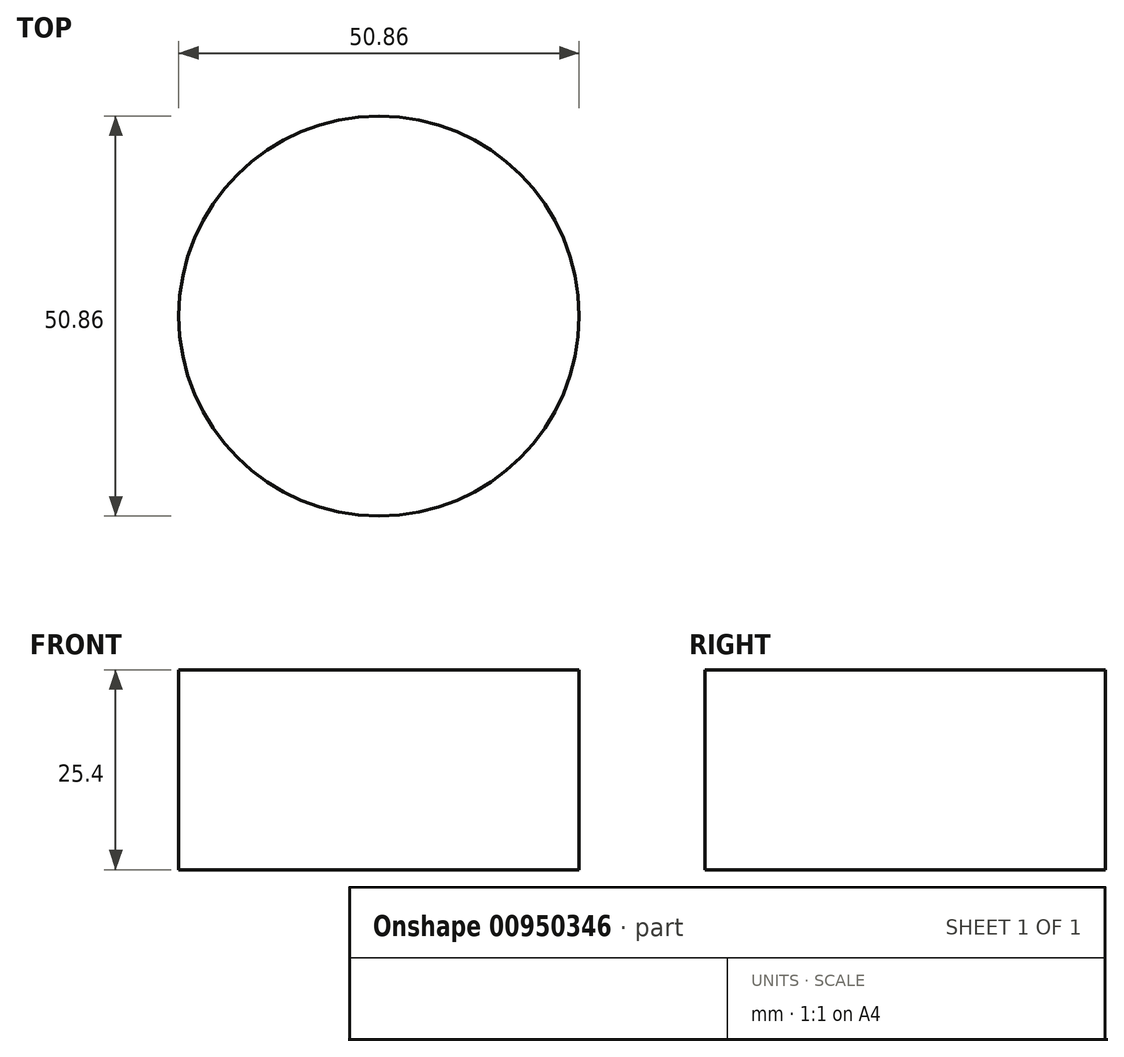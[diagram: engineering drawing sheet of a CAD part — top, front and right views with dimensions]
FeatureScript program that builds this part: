
annotation { "Feature Type Name" : "Feature", "Feature Type Description" : "" }
export const myFeature = defineFeature(function(context is Context, id is Id, definition is map)
    precondition{}
    {
        {
            var Q0;
            Q0=qCreatedBy(makeId("Top.planeOp"),FACE);
            var sketch = newSketch(context, id + "F0", { "sketchPlane" : qUnion([Q0])});
            skCircle(sketch, "E0", {"center": v(0, 0) * mm, "radius": 25.43 * mm});
            skSolve(sketch);
        }
        {
            var Q0;
            Q0=makeQuery(id+"F0.imprint","IMPRINT",FACE,{"disambiguationData":[TD([[makeQuery(id+"F0.imprint","IMPRINT",EDGE,{"derivedFrom":sQuery(id+"F0.wireOp",EDGE,"E0")}),1.0]])]});
            extrude(context, id + "F1", {"entities" : qUnion([Q0]), "depth" : 25.4 * mm, "offsetDistance" : 25.4 * mm});
        }
    });
